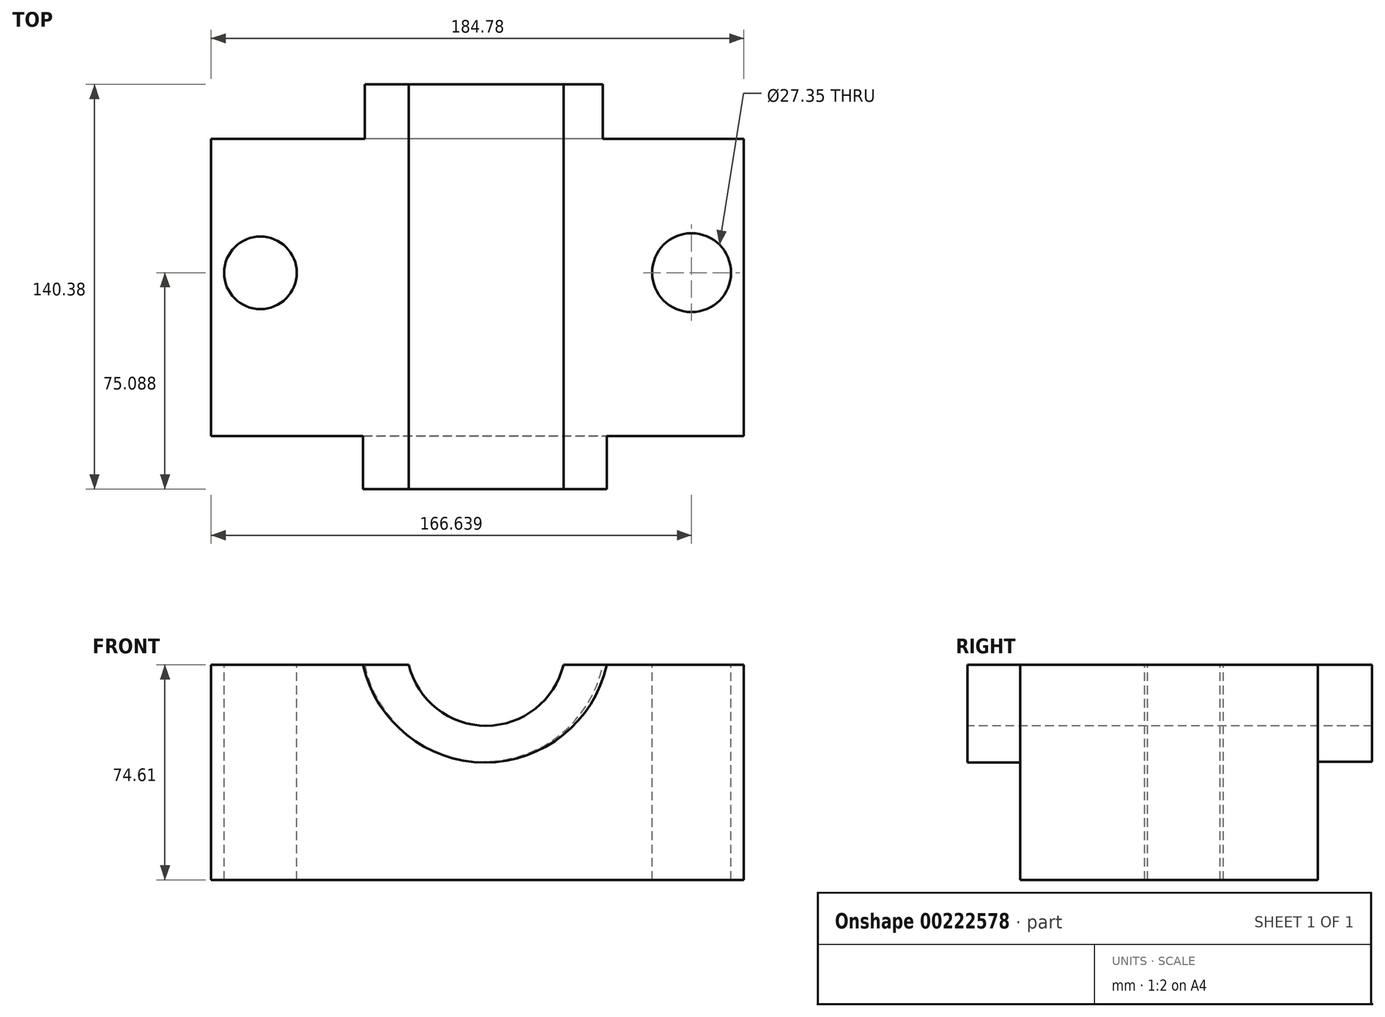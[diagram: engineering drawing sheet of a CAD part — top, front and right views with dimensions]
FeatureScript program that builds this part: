
annotation { "Feature Type Name" : "Feature", "Feature Type Description" : "" }
export const myFeature = defineFeature(function(context is Context, id is Id, definition is map)
    precondition{}
    {
        {
            var Q0;
            Q0=qCreatedBy(makeId("Top.planeOp"),FACE);
            var sketch = newSketch(context, id + "F0", { "sketchPlane" : qUnion([Q0])});
            skLineSegment(sketch, "E0.bottom", {"start": v(92.39, -87.88) * mm, "end": v(-92.39, -87.88) * mm});
            skLineSegment(sketch, "E0.top", {"start": v(92.39, 15.34) * mm, "end": v(-92.39, 15.34) * mm});
            skLineSegment(sketch, "E0.left", {"start": v(92.39, -87.88) * mm, "end": v(92.39, 15.34) * mm});
            skLineSegment(sketch, "E0.right", {"start": v(-92.39, -87.88) * mm, "end": v(-92.39, 15.34) * mm});
            skPoint(sketch, "E0.middle", {"position": v(0, -36.27) * mm});
            skSolve(sketch);
        }
        {
            var Q0;
            Q0 = qSketchRegion(id + "F0", true);
            extrude(context, id + "F1", {"entities" : qUnion([Q0]), "depth" : 74.61 * mm});
        }
        {
            var Q0;
            Q0=makeQuery(id+"F1.opExtrude","SWEPT_FACE",FACE,{"disambiguationData":[OSD([sQuery(id+"F0.wireOp",EDGE,"E0.bottom")])]});
            var sketch = newSketch(context, id + "F2", { "sketchPlane" : qUnion([Q0])});
            skArc(sketch, "E1", {"start": v(-39.7, 74.61) * mm, "mid": v(2.58, 40.74) * mm, "end": v(44.85, 74.61) * mm});
            skSolve(sketch);
        }
        {
            var Q0;
            {var subQ0=sQuery(id+"F2.wireOp",EDGE,"E1");Q0=makeQuery(id+"F2.imprint","IMPRINT",FACE,{"disambiguationData":[TD([[makeQuery(id+"F2.imprint","IMPRINT",EDGE,{"derivedFrom":subQ0}),1.0]])]});}
            extrude(context, id + "F3", {"entities" : qUnion([Q0]), "operationType" : NewBodyOperationType.ADD, "depth" : 18.34 * mm});
        }
        {
            var Q0;
            Q0=makeQuery(id+"F1.opExtrude","SWEPT_FACE",FACE,{"disambiguationData":[OSD([sQuery(id+"F0.wireOp",EDGE,"E0.top")])]});
            var sketch = newSketch(context, id + "F4", { "sketchPlane" : qUnion([Q0])});
            skArc(sketch, "E2", {"start": v(-43.51, 74.61) * mm, "mid": v(-2.18, 41.02) * mm, "end": v(39.15, 74.61) * mm});
            skSolve(sketch);
        }
        {
            var Q0;
            {var subQ0=sQuery(id+"F4.wireOp",EDGE,"E2");Q0=makeQuery(id+"F4.imprint","IMPRINT",FACE,{"disambiguationData":[TD([[makeQuery(id+"F4.imprint","IMPRINT",EDGE,{"derivedFrom":subQ0}),1.0]])]});}
            extrude(context, id + "F5", {"entities" : qUnion([Q0]), "operationType" : NewBodyOperationType.ADD, "depth" : 18.82 * mm});
        }
        {
            var Q0;
            Q0=makeQuery(id+"F3.opExtrude","CAP_FACE",FACE,{"disambiguationData":[OSD([sQuery(id+"F0.wireOp",EDGE,"E0.bottom"),sQuery(id+"F2.wireOp",EDGE,"E1")])],"isStart":false});
            var sketch = newSketch(context, id + "F6", { "sketchPlane" : qUnion([Q0])});
            skArc(sketch, "E3", {"start": v(-23.81, 74.61) * mm, "mid": v(3, 53.47) * mm, "end": v(29.81, 74.61) * mm});
            skSolve(sketch);
        }
        {
            var Q0;
            {var subQ0=sQuery(id+"F6.wireOp",EDGE,"E3");Q0=makeQuery(id+"F6.imprint","IMPRINT",FACE,{"disambiguationData":[TD([[makeQuery(id+"F6.imprint","IMPRINT",EDGE,{"derivedFrom":subQ0}),1.0]])]});}
            extrude(context, id + "F7", {"entities" : qUnion([Q0]), "operationType" : NewBodyOperationType.REMOVE, "endBound" : BoundingType.THROUGH_ALL, "oppositeDirection" : true, "depth" : 25.4 * mm});
        }
        {
            var Q0;
            {var subQ0=sQuery(id+"F0.wireOp",EDGE,"E0.right");var subQ2=sQuery(id+"F0.wireOp",EDGE,"E0.top");var subQ3=sQuery(id+"F0.wireOp",EDGE,"E0.bottom");Q0=makeQuery(id+"F7.boolean.opBoolean","SPLIT",FACE,{"disambiguationData":[TD([makeQuery(id+"F1.opExtrude","SWEPT_FACE",FACE,{"disambiguationData":[OSD([subQ0])]})])],"derivedFrom":makeQuery(id+"F5.boolean.opBoolean","MERGE",FACE,{"derivedFrom":[makeQuery(id+"F3.boolean.opBoolean","MERGE",FACE,{"derivedFrom":[makeQuery(id+"F1.opExtrude","CAP_FACE",FACE,{"disambiguationData":[OSD([subQ3,subQ2,sQuery(id+"F0.wireOp",EDGE,"E0.left"),subQ0])],"isStart":false}),makeQuery(id+"F3.opExtrude","SWEPT_FACE",FACE,{"disambiguationData":[OSD([subQ3])]})]}),makeQuery(id+"F5.opExtrude","SWEPT_FACE",FACE,{"disambiguationData":[OSD([subQ2])]})]})});}
            var sketch = newSketch(context, id + "F8", { "sketchPlane" : qUnion([Q0])});
            skCircle(sketch, "E4", {"center": v(-75.3, -31.19) * mm, "radius": 12.6 * mm});
            skSolve(sketch);
        }
        {
            var Q0;
            Q0 = qSketchRegion(id + "F8", true);
            extrude(context, id + "F9", {"entities" : qUnion([Q0]), "operationType" : NewBodyOperationType.REMOVE, "endBound" : BoundingType.THROUGH_ALL, "oppositeDirection" : true, "depth" : 25.4 * mm});
        }
        {
            var Q0;
            {var subQ0=sQuery(id+"F0.wireOp",EDGE,"E0.left");var subQ2=sQuery(id+"F0.wireOp",EDGE,"E0.top");var subQ4=sQuery(id+"F0.wireOp",EDGE,"E0.bottom");Q0=makeQuery(id+"F7.boolean.opBoolean","SPLIT",FACE,{"disambiguationData":[TD([makeQuery(id+"F1.opExtrude","SWEPT_FACE",FACE,{"disambiguationData":[OSD([subQ0])]})])],"derivedFrom":makeQuery(id+"F5.boolean.opBoolean","MERGE",FACE,{"derivedFrom":[makeQuery(id+"F3.boolean.opBoolean","MERGE",FACE,{"derivedFrom":[makeQuery(id+"F1.opExtrude","CAP_FACE",FACE,{"disambiguationData":[OSD([subQ4,subQ2,subQ0,sQuery(id+"F0.wireOp",EDGE,"E0.right")])],"isStart":false}),makeQuery(id+"F3.opExtrude","SWEPT_FACE",FACE,{"disambiguationData":[OSD([subQ4])]})]}),makeQuery(id+"F5.opExtrude","SWEPT_FACE",FACE,{"disambiguationData":[OSD([subQ2])]})]})});}
            var sketch = newSketch(context, id + "F10", { "sketchPlane" : qUnion([Q0])});
            skCircle(sketch, "E5", {"center": v(74.25, -31.13) * mm, "radius": 13.67 * mm});
            skSolve(sketch);
        }
        {
            var Q0;
            Q0 = qSketchRegion(id + "F10", true);
            extrude(context, id + "F11", {"entities" : qUnion([Q0]), "operationType" : NewBodyOperationType.REMOVE, "endBound" : BoundingType.THROUGH_ALL, "oppositeDirection" : true, "depth" : 25.4 * mm});
        }
    });
